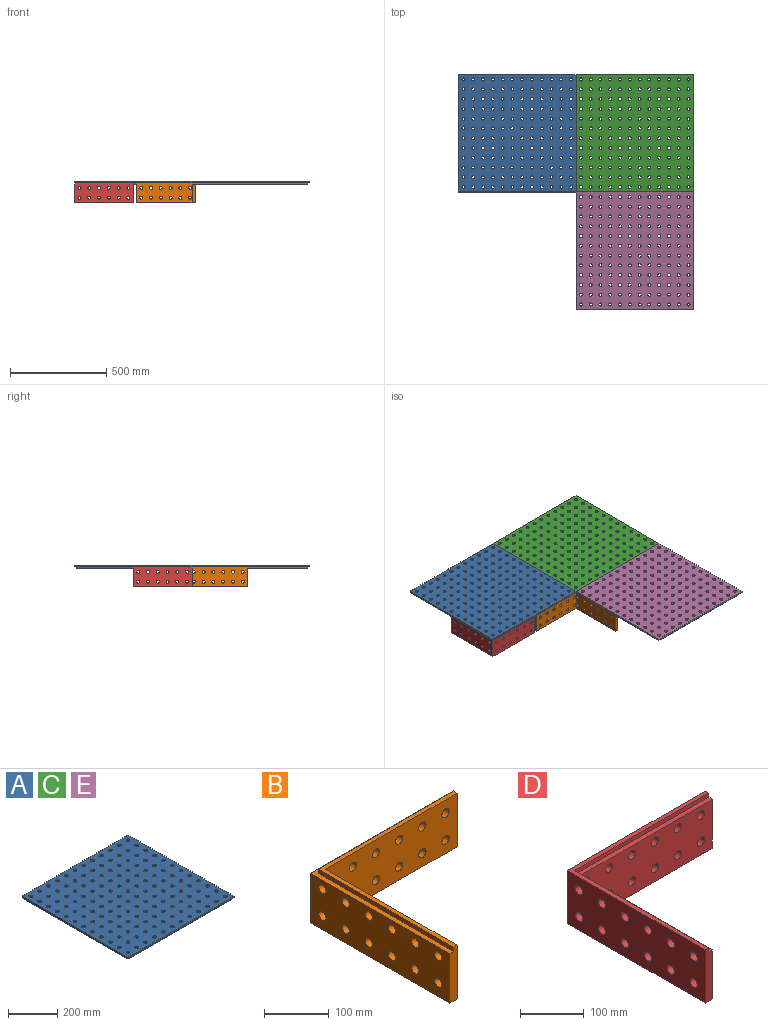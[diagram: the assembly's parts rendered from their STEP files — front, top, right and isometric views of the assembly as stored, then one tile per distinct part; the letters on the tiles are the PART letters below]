
ASSEMBLY  parts=5 mates=4
PART A: 155 faces, bbox 609.6x609.6x15.9 mm
  f0: plane 593.73x593.73mm, normal (0,0,-1), area 324007.1mm2, adj f6,f7,f8,f9,f10,f11,f12,f13
  f1: plane 609.6x7.94mm, normal (1,0,0), area 4838.7mm2, adj f2,f4,f5,f154
  f2: plane 609.6x7.94mm, normal (0,1,0), area 4838.7mm2, adj f1,f3,f5,f154
  f3: plane 609.6x7.94mm, normal (-1,0,0), area 4838.7mm2, adj f2,f4,f5,f154
  f4: plane 609.6x7.94mm, normal (0,-1,0), area 4838.7mm2, adj f1,f3,f5,f154
  f5: plane 609.6x609.6mm, normal (0,0,1), area 343109.9mm2, adj f1,f2,f3,f4,f6,f7,f8,f9
  f6: cylinder r=7.94mm len=15.88mm, axis (0,0,1), area 791.7mm2, adj f0,f5
  f7: cylinder r=7.94mm len=15.88mm, axis (0,0,1), area 791.7mm2, adj f0,f5
  f8: cylinder r=7.94mm len=15.88mm, axis (0,0,1), area 791.7mm2, adj f0,f5
  f9: cylinder r=7.94mm len=15.88mm, axis (0,0,1), area 791.7mm2, adj f0,f5
  f10: cylinder r=7.94mm len=15.88mm, axis (0,0,1), area 791.7mm2, adj f0,f5
  f11: cylinder r=7.94mm len=15.88mm, axis (0,0,1), area 791.7mm2, adj f0,f5
  f12: cylinder r=7.94mm len=15.88mm, axis (0,0,1), area 791.7mm2, adj f0,f5
  f13: cylinder r=7.94mm len=15.88mm, axis (0,0,1), area 791.7mm2, adj f0,f5
  f14: cylinder r=7.94mm len=15.88mm, axis (0,0,1), area 791.7mm2, adj f0,f5
  f15: cylinder r=7.94mm len=15.88mm, axis (0,0,1), area 791.7mm2, adj f0,f5
  f16: cylinder r=7.94mm len=15.88mm, axis (0,0,1), area 791.7mm2, adj f0,f5
  f17: cylinder r=7.94mm len=15.88mm, axis (0,0,1), area 791.7mm2, adj f0,f5
  f18: cylinder r=7.94mm len=15.88mm, axis (0,0,1), area 791.7mm2, adj f0,f5
  f19: cylinder r=7.94mm len=15.88mm, axis (0,0,1), area 791.7mm2, adj f0,f5
  f20: cylinder r=7.94mm len=15.88mm, axis (0,0,1), area 791.7mm2, adj f0,f5
  f21: cylinder r=7.94mm len=15.88mm, axis (0,0,1), area 791.7mm2, adj f0,f5
  f22: cylinder r=7.94mm len=15.88mm, axis (0,0,1), area 791.7mm2, adj f0,f5
  f23: cylinder r=7.94mm len=15.88mm, axis (0,0,1), area 791.7mm2, adj f0,f5
  f24: cylinder r=7.94mm len=15.88mm, axis (0,0,1), area 791.7mm2, adj f0,f5
  f25: cylinder r=7.94mm len=15.88mm, axis (0,0,1), area 791.7mm2, adj f0,f5
  f26: cylinder r=7.94mm len=15.88mm, axis (0,0,1), area 791.7mm2, adj f0,f5
  f27: cylinder r=7.94mm len=15.88mm, axis (0,0,1), area 791.7mm2, adj f0,f5
  f28: cylinder r=7.94mm len=15.88mm, axis (0,0,1), area 791.7mm2, adj f0,f5
  f29: cylinder r=7.94mm len=15.88mm, axis (0,0,1), area 791.7mm2, adj f0,f5
  f30: cylinder r=7.94mm len=15.88mm, axis (0,0,1), area 791.7mm2, adj f0,f5
  f31: cylinder r=7.94mm len=15.88mm, axis (0,0,1), area 791.7mm2, adj f0,f5
  f32: cylinder r=7.94mm len=15.88mm, axis (0,0,1), area 791.7mm2, adj f0,f5
  f33: cylinder r=7.94mm len=15.88mm, axis (0,0,1), area 791.7mm2, adj f0,f5
  f34: cylinder r=7.94mm len=15.88mm, axis (0,0,1), area 791.7mm2, adj f0,f5
  f35: cylinder r=7.94mm len=15.88mm, axis (0,0,1), area 791.7mm2, adj f0,f5
  f36: cylinder r=7.94mm len=15.88mm, axis (0,0,1), area 791.7mm2, adj f0,f5
  f37: cylinder r=7.94mm len=15.88mm, axis (0,0,1), area 791.7mm2, adj f0,f5
  f38: cylinder r=7.94mm len=15.88mm, axis (0,0,1), area 791.7mm2, adj f0,f5
  f39: cylinder r=7.94mm len=15.88mm, axis (0,0,1), area 791.7mm2, adj f0,f5
  f40: cylinder r=7.94mm len=15.88mm, axis (0,0,1), area 791.7mm2, adj f0,f5
  f41: cylinder r=7.94mm len=15.88mm, axis (0,0,1), area 791.7mm2, adj f0,f5
  f42: cylinder r=7.94mm len=15.88mm, axis (0,0,1), area 791.7mm2, adj f0,f5
  f43: cylinder r=7.94mm len=15.88mm, axis (0,0,1), area 791.7mm2, adj f0,f5
  f44: cylinder r=7.94mm len=15.88mm, axis (0,0,1), area 791.7mm2, adj f0,f5
  f45: cylinder r=7.94mm len=15.88mm, axis (0,0,1), area 791.7mm2, adj f0,f5
  f46: cylinder r=7.94mm len=15.88mm, axis (0,0,1), area 791.7mm2, adj f0,f5
  f47: cylinder r=7.94mm len=15.88mm, axis (0,0,1), area 791.7mm2, adj f0,f5
  f48: cylinder r=7.94mm len=15.88mm, axis (0,0,1), area 791.7mm2, adj f0,f5
  f49: cylinder r=7.94mm len=15.88mm, axis (0,0,1), area 791.7mm2, adj f0,f5
  f50: cylinder r=7.94mm len=15.88mm, axis (0,0,1), area 791.7mm2, adj f0,f5
  f51: cylinder r=7.94mm len=15.88mm, axis (0,0,1), area 791.7mm2, adj f0,f5
  f52: cylinder r=7.94mm len=15.88mm, axis (0,0,1), area 791.7mm2, adj f0,f5
  f53: cylinder r=7.94mm len=15.88mm, axis (0,0,1), area 791.7mm2, adj f0,f5
  f54: cylinder r=7.94mm len=15.88mm, axis (0,0,1), area 791.7mm2, adj f0,f5
  f55: cylinder r=7.94mm len=15.88mm, axis (0,0,1), area 791.7mm2, adj f0,f5
  f56: cylinder r=7.94mm len=15.88mm, axis (0,0,1), area 791.7mm2, adj f0,f5
  f57: cylinder r=7.94mm len=15.88mm, axis (0,0,1), area 791.7mm2, adj f0,f5
  f58: cylinder r=7.94mm len=15.88mm, axis (0,0,1), area 791.7mm2, adj f0,f5
  f59: cylinder r=7.94mm len=15.88mm, axis (0,0,1), area 791.7mm2, adj f0,f5
  f60: cylinder r=7.94mm len=15.88mm, axis (0,0,1), area 791.7mm2, adj f0,f5
  f61: cylinder r=7.94mm len=15.88mm, axis (0,0,1), area 791.7mm2, adj f0,f5
  f62: cylinder r=7.94mm len=15.88mm, axis (0,0,1), area 791.7mm2, adj f0,f5
  f63: cylinder r=7.94mm len=15.88mm, axis (0,0,1), area 791.7mm2, adj f0,f5
  f64: cylinder r=7.94mm len=15.88mm, axis (0,0,1), area 791.7mm2, adj f0,f5
  f65: cylinder r=7.94mm len=15.88mm, axis (0,0,1), area 791.7mm2, adj f0,f5
  f66: cylinder r=7.94mm len=15.88mm, axis (0,0,1), area 791.7mm2, adj f0,f5
  f67: cylinder r=7.94mm len=15.88mm, axis (0,0,1), area 791.7mm2, adj f0,f5
  f68: cylinder r=7.94mm len=15.88mm, axis (0,0,1), area 791.7mm2, adj f0,f5
  f69: cylinder r=7.94mm len=15.88mm, axis (0,0,1), area 791.7mm2, adj f0,f5
  f70: cylinder r=7.94mm len=15.88mm, axis (0,0,1), area 791.7mm2, adj f0,f5
  f71: cylinder r=7.94mm len=15.88mm, axis (0,0,1), area 791.7mm2, adj f0,f5
  f72: cylinder r=7.94mm len=15.88mm, axis (0,0,1), area 791.7mm2, adj f0,f5
  f73: cylinder r=7.94mm len=15.88mm, axis (0,0,1), area 791.7mm2, adj f0,f5
  f74: cylinder r=7.94mm len=15.88mm, axis (0,0,1), area 791.7mm2, adj f0,f5
  f75: cylinder r=7.94mm len=15.88mm, axis (0,0,1), area 791.7mm2, adj f0,f5
  f76: cylinder r=7.94mm len=15.88mm, axis (0,0,1), area 791.7mm2, adj f0,f5
  f77: cylinder r=7.94mm len=15.88mm, axis (0,0,1), area 791.7mm2, adj f0,f5
  f78: cylinder r=7.94mm len=15.88mm, axis (0,0,1), area 791.7mm2, adj f0,f5
  f79: cylinder r=7.94mm len=15.88mm, axis (0,0,1), area 791.7mm2, adj f0,f5
  f80: cylinder r=7.94mm len=15.88mm, axis (0,0,1), area 791.7mm2, adj f0,f5
  f81: cylinder r=7.94mm len=15.88mm, axis (0,0,1), area 791.7mm2, adj f0,f5
  f82: cylinder r=7.94mm len=15.88mm, axis (0,0,1), area 791.7mm2, adj f0,f5
  f83: cylinder r=7.94mm len=15.88mm, axis (0,0,1), area 791.7mm2, adj f0,f5
  f84: cylinder r=7.94mm len=15.88mm, axis (0,0,1), area 791.7mm2, adj f0,f5
  f85: cylinder r=7.94mm len=15.88mm, axis (0,0,1), area 791.7mm2, adj f0,f5
  f86: cylinder r=7.94mm len=15.88mm, axis (0,0,1), area 791.7mm2, adj f0,f5
  f87: cylinder r=7.94mm len=15.88mm, axis (0,0,1), area 791.7mm2, adj f0,f5
  f88: cylinder r=7.94mm len=15.88mm, axis (0,0,1), area 791.7mm2, adj f0,f5
  f89: cylinder r=7.94mm len=15.88mm, axis (0,0,1), area 791.7mm2, adj f0,f5
  f90: cylinder r=7.94mm len=15.88mm, axis (0,0,1), area 791.7mm2, adj f0,f5
  f91: cylinder r=7.94mm len=15.88mm, axis (0,0,1), area 791.7mm2, adj f0,f5
  f92: cylinder r=7.94mm len=15.88mm, axis (0,0,1), area 791.7mm2, adj f0,f5
  f93: cylinder r=7.94mm len=15.88mm, axis (0,0,1), area 791.7mm2, adj f0,f5
  f94: cylinder r=7.94mm len=15.88mm, axis (0,0,1), area 791.7mm2, adj f0,f5
  f95: cylinder r=7.94mm len=15.88mm, axis (0,0,1), area 791.7mm2, adj f0,f5
  f96: cylinder r=7.94mm len=15.88mm, axis (0,0,1), area 791.7mm2, adj f0,f5
  f97: cylinder r=7.94mm len=15.88mm, axis (0,0,1), area 791.7mm2, adj f0,f5
  f98: cylinder r=7.94mm len=15.88mm, axis (0,0,1), area 791.7mm2, adj f0,f5
  f99: cylinder r=7.94mm len=15.88mm, axis (0,0,1), area 791.7mm2, adj f0,f5
  f100: cylinder r=7.94mm len=15.88mm, axis (0,0,1), area 791.7mm2, adj f0,f5
  f101: cylinder r=7.94mm len=15.88mm, axis (0,0,1), area 791.7mm2, adj f0,f5
  f102: cylinder r=7.94mm len=15.88mm, axis (0,0,1), area 791.7mm2, adj f0,f5
  f103: cylinder r=7.94mm len=15.88mm, axis (0,0,1), area 791.7mm2, adj f0,f5
  f104: cylinder r=7.94mm len=15.88mm, axis (0,0,1), area 791.7mm2, adj f0,f5
  f105: cylinder r=7.94mm len=15.88mm, axis (0,0,1), area 791.7mm2, adj f0,f5
  f106: cylinder r=7.94mm len=15.88mm, axis (0,0,1), area 791.7mm2, adj f0,f5
  f107: cylinder r=7.94mm len=15.88mm, axis (0,0,1), area 791.7mm2, adj f0,f5
  f108: cylinder r=7.94mm len=15.88mm, axis (0,0,1), area 791.7mm2, adj f0,f5
  f109: cylinder r=7.94mm len=15.88mm, axis (0,0,1), area 791.7mm2, adj f0,f5
  f110: cylinder r=7.94mm len=15.88mm, axis (0,0,1), area 791.7mm2, adj f0,f5
  f111: cylinder r=7.94mm len=15.88mm, axis (0,0,1), area 791.7mm2, adj f0,f5
  f112: cylinder r=7.94mm len=15.88mm, axis (0,0,1), area 791.7mm2, adj f0,f5
  f113: cylinder r=7.94mm len=15.88mm, axis (0,0,1), area 791.7mm2, adj f0,f5
  f114: cylinder r=7.94mm len=15.88mm, axis (0,0,1), area 791.7mm2, adj f0,f5
  f115: cylinder r=7.94mm len=15.88mm, axis (0,0,1), area 791.7mm2, adj f0,f5
  f116: cylinder r=7.94mm len=15.88mm, axis (0,0,1), area 791.7mm2, adj f0,f5
  f117: cylinder r=7.94mm len=15.88mm, axis (0,0,1), area 791.7mm2, adj f0,f5
  f118: cylinder r=7.94mm len=15.88mm, axis (0,0,1), area 791.7mm2, adj f0,f5
  f119: cylinder r=7.94mm len=15.88mm, axis (0,0,1), area 791.7mm2, adj f0,f5
  f120: cylinder r=7.94mm len=15.88mm, axis (0,0,1), area 791.7mm2, adj f0,f5
  f121: cylinder r=7.94mm len=15.88mm, axis (0,0,1), area 791.7mm2, adj f0,f5
  f122: cylinder r=7.94mm len=15.88mm, axis (0,0,1), area 791.7mm2, adj f0,f5
  f123: cylinder r=7.94mm len=15.88mm, axis (0,0,1), area 791.7mm2, adj f0,f5
  f124: cylinder r=7.94mm len=15.88mm, axis (0,0,1), area 791.7mm2, adj f0,f5
  f125: cylinder r=7.94mm len=15.88mm, axis (0,0,1), area 791.7mm2, adj f0,f5
  f126: cylinder r=7.94mm len=15.88mm, axis (0,0,1), area 791.7mm2, adj f0,f5
  f127: cylinder r=7.94mm len=15.88mm, axis (0,0,1), area 791.7mm2, adj f0,f5
  f128: cylinder r=7.94mm len=15.88mm, axis (0,0,1), area 791.7mm2, adj f0,f5
  f129: cylinder r=7.94mm len=15.88mm, axis (0,0,1), area 791.7mm2, adj f0,f5
  f130: cylinder r=7.94mm len=15.88mm, axis (0,0,1), area 791.7mm2, adj f0,f5
  f131: cylinder r=7.94mm len=15.88mm, axis (0,0,1), area 791.7mm2, adj f0,f5
  f132: cylinder r=7.94mm len=15.88mm, axis (0,0,1), area 791.7mm2, adj f0,f5
  f133: cylinder r=7.94mm len=15.88mm, axis (0,0,1), area 791.7mm2, adj f0,f5
  f134: cylinder r=7.94mm len=15.88mm, axis (0,0,1), area 791.7mm2, adj f0,f5
  f135: cylinder r=7.94mm len=15.88mm, axis (0,0,1), area 791.7mm2, adj f0,f5
  f136: cylinder r=7.94mm len=15.88mm, axis (0,0,1), area 791.7mm2, adj f0,f5
  f137: cylinder r=7.94mm len=15.88mm, axis (0,0,1), area 791.7mm2, adj f0,f5
  f138: cylinder r=7.94mm len=15.88mm, axis (0,0,1), area 791.7mm2, adj f0,f5
  f139: cylinder r=7.94mm len=15.88mm, axis (0,0,1), area 791.7mm2, adj f0,f5
  f140: cylinder r=7.94mm len=15.88mm, axis (0,0,1), area 791.7mm2, adj f0,f5
  f141: cylinder r=7.94mm len=15.88mm, axis (0,0,1), area 791.7mm2, adj f0,f5
  f142: cylinder r=7.94mm len=15.88mm, axis (0,0,1), area 791.7mm2, adj f0,f5
  f143: cylinder r=7.94mm len=15.88mm, axis (0,0,1), area 791.7mm2, adj f0,f5
  f144: cylinder r=7.94mm len=15.88mm, axis (0,0,1), area 791.7mm2, adj f0,f5
  f145: cylinder r=7.94mm len=15.88mm, axis (0,0,1), area 791.7mm2, adj f0,f5
  f146: cylinder r=7.94mm len=15.88mm, axis (0,0,1), area 791.7mm2, adj f0,f5
  f147: cylinder r=7.94mm len=15.88mm, axis (0,0,1), area 791.7mm2, adj f0,f5
  f148: cylinder r=7.94mm len=15.88mm, axis (0,0,1), area 791.7mm2, adj f0,f5
  f149: cylinder r=7.94mm len=15.88mm, axis (0,0,1), area 791.7mm2, adj f0,f5
  f150: plane 593.73x7.94mm, normal (0,-1,0), area 4712.7mm2, adj f0,f151,f153,f154
  f151: plane 593.73x7.94mm, normal (1,0,0), area 4712.7mm2, adj f0,f150,f152,f154
  f152: plane 593.73x7.94mm, normal (0,1,0), area 4712.7mm2, adj f0,f151,f153,f154
  f153: plane 593.73x7.94mm, normal (-1,0,0), area 4712.7mm2, adj f0,f150,f152,f154
  f154: plane 609.6x609.6mm, normal (0,0,-1), area 19102.8mm2, adj f1,f2,f3,f4,f150,f151,f152,f153
PART B: 35 faces, bbox 304.8x304.8x101.6 mm
  f0: plane 304.8x93.66mm, normal (0,1,0), area 26173.1mm2, adj f1,f3,f7,f20,f21,f22,f23,f24
  f1: plane 304.8x93.66mm, normal (-1,0,0), area 26173.1mm2, adj f0,f4,f7,f8,f9,f10,f11,f12
  f2: plane 296.86x296.86mm, normal (0,0,1), area 4649.7mm2, adj f3,f4,f5,f6,f32,f33
  f3: plane 101.6x15.88mm, normal (1,0,0), area 1549.9mm2, adj f0,f2,f6,f7,f33,f34
  f4: plane 101.6x15.88mm, normal (0,-1,0), area 1549.9mm2, adj f1,f2,f5,f7,f32,f34
  f5: plane 288.93x101.6mm, normal (1,0,0), area 26979.6mm2, adj f2,f4,f6,f7,f8,f9,f10,f11
  f6: plane 288.93x101.6mm, normal (0,-1,0), area 26979.6mm2, adj f2,f3,f5,f7,f20,f21,f22,f23
  f7: plane 304.8x304.8mm, normal (0,0,-1), area 9425.4mm2, adj f0,f1,f3,f4,f5,f6
  f8: cylinder r=7.94mm len=15.88mm, axis (-1,0,0), area 791.7mm2, adj f1,f5
  f9: cylinder r=7.94mm len=15.88mm, axis (-1,0,0), area 791.7mm2, adj f1,f5
  f10: cylinder r=7.94mm len=15.88mm, axis (-1,0,0), area 791.7mm2, adj f1,f5
  f11: cylinder r=7.94mm len=15.88mm, axis (-1,0,0), area 791.7mm2, adj f1,f5
  f12: cylinder r=7.94mm len=15.88mm, axis (-1,0,0), area 791.7mm2, adj f1,f5
  f13: cylinder r=7.94mm len=15.88mm, axis (-1,0,0), area 791.7mm2, adj f1,f5
  f14: cylinder r=7.94mm len=15.88mm, axis (-1,0,0), area 791.7mm2, adj f1,f5
  f15: cylinder r=7.94mm len=15.88mm, axis (-1,0,0), area 791.7mm2, adj f1,f5
  f16: cylinder r=7.94mm len=15.88mm, axis (-1,0,0), area 791.7mm2, adj f1,f5
  f17: cylinder r=7.94mm len=15.88mm, axis (-1,0,0), area 791.7mm2, adj f1,f5
  f18: cylinder r=7.94mm len=15.88mm, axis (-1,0,0), area 791.7mm2, adj f1,f5
  f19: cylinder r=7.94mm len=15.88mm, axis (-1,0,0), area 791.7mm2, adj f1,f5
  f20: cylinder r=7.94mm len=15.88mm, axis (0,1,0), area 791.7mm2, adj f0,f6
  f21: cylinder r=7.94mm len=15.88mm, axis (0,1,0), area 791.7mm2, adj f0,f6
  f22: cylinder r=7.94mm len=15.88mm, axis (0,1,0), area 791.7mm2, adj f0,f6
  f23: cylinder r=7.94mm len=15.88mm, axis (0,1,0), area 791.7mm2, adj f0,f6
  f24: cylinder r=7.94mm len=15.88mm, axis (0,1,0), area 791.7mm2, adj f0,f6
  f25: cylinder r=7.94mm len=15.88mm, axis (0,1,0), area 791.7mm2, adj f0,f6
  f26: cylinder r=7.94mm len=15.88mm, axis (0,1,0), area 791.7mm2, adj f0,f6
  f27: cylinder r=7.94mm len=15.88mm, axis (0,1,0), area 791.7mm2, adj f0,f6
  f28: cylinder r=7.94mm len=15.88mm, axis (0,1,0), area 791.7mm2, adj f0,f6
  f29: cylinder r=7.94mm len=15.88mm, axis (0,1,0), area 791.7mm2, adj f0,f6
  f30: cylinder r=7.94mm len=15.88mm, axis (0,1,0), area 791.7mm2, adj f0,f6
  f31: cylinder r=7.94mm len=15.88mm, axis (0,1,0), area 791.7mm2, adj f0,f6
  f32: plane 296.86x7.94mm, normal (-1,0,0), area 2356.3mm2, adj f2,f4,f33,f34
  f33: plane 296.86x7.94mm, normal (0,1,0), area 2356.3mm2, adj f2,f3,f32,f34
  f34: plane 304.8x304.8mm, normal (0,0,1), area 4775.7mm2, adj f0,f1,f3,f4,f32,f33
PART C: same geometry as A
PART D: 35 faces, bbox 304.8x304.8x101.6 mm
  f0: plane 101.6x15.88mm, normal (1,0,0), area 1549.9mm2, adj f2,f3,f6,f7,f32,f34
  f1: plane 288.93x93.66mm, normal (1,0,0), area 24686.2mm2, adj f2,f5,f7,f8,f9,f10,f11,f12
  f2: plane 288.93x93.66mm, normal (0,-1,0), area 24686.2mm2, adj f0,f1,f7,f20,f21,f22,f23,f24
  f3: plane 304.8x101.6mm, normal (0,1,0), area 28592.5mm2, adj f0,f4,f6,f7,f20,f21,f22,f23
  f4: plane 304.8x101.6mm, normal (-1,0,0), area 28592.5mm2, adj f3,f5,f6,f7,f8,f9,f10,f11
  f5: plane 101.6x15.88mm, normal (0,-1,0), area 1549.9mm2, adj f1,f4,f6,f7,f33,f34
  f6: plane 304.8x304.8mm, normal (0,0,1), area 4775.7mm2, adj f0,f3,f4,f5,f32,f33
  f7: plane 304.8x304.8mm, normal (0,0,-1), area 9425.4mm2, adj f0,f1,f2,f3,f4,f5
  f8: cylinder r=7.94mm len=15.88mm, axis (-1,0,0), area 791.7mm2, adj f1,f4
  f9: cylinder r=7.94mm len=15.88mm, axis (-1,0,0), area 791.7mm2, adj f1,f4
  f10: cylinder r=7.94mm len=15.88mm, axis (-1,0,0), area 791.7mm2, adj f1,f4
  f11: cylinder r=7.94mm len=15.88mm, axis (-1,0,0), area 791.7mm2, adj f1,f4
  f12: cylinder r=7.94mm len=15.88mm, axis (-1,0,0), area 791.7mm2, adj f1,f4
  f13: cylinder r=7.94mm len=15.88mm, axis (-1,0,0), area 791.7mm2, adj f1,f4
  f14: cylinder r=7.94mm len=15.88mm, axis (-1,0,0), area 791.7mm2, adj f1,f4
  f15: cylinder r=7.94mm len=15.88mm, axis (-1,0,0), area 791.7mm2, adj f1,f4
  f16: cylinder r=7.94mm len=15.88mm, axis (-1,0,0), area 791.7mm2, adj f1,f4
  f17: cylinder r=7.94mm len=15.88mm, axis (-1,0,0), area 791.7mm2, adj f1,f4
  f18: cylinder r=7.94mm len=15.88mm, axis (-1,0,0), area 791.7mm2, adj f1,f4
  f19: cylinder r=7.94mm len=15.88mm, axis (-1,0,0), area 791.7mm2, adj f1,f4
  f20: cylinder r=7.94mm len=15.88mm, axis (0,1,0), area 791.7mm2, adj f2,f3
  f21: cylinder r=7.94mm len=15.88mm, axis (0,1,0), area 791.7mm2, adj f2,f3
  f22: cylinder r=7.94mm len=15.88mm, axis (0,1,0), area 791.7mm2, adj f2,f3
  f23: cylinder r=7.94mm len=15.88mm, axis (0,1,0), area 791.7mm2, adj f2,f3
  f24: cylinder r=7.94mm len=15.88mm, axis (0,1,0), area 791.7mm2, adj f2,f3
  f25: cylinder r=7.94mm len=15.88mm, axis (0,1,0), area 791.7mm2, adj f2,f3
  f26: cylinder r=7.94mm len=15.88mm, axis (0,1,0), area 791.7mm2, adj f2,f3
  f27: cylinder r=7.94mm len=15.88mm, axis (0,1,0), area 791.7mm2, adj f2,f3
  f28: cylinder r=7.94mm len=15.88mm, axis (0,1,0), area 791.7mm2, adj f2,f3
  f29: cylinder r=7.94mm len=15.88mm, axis (0,1,0), area 791.7mm2, adj f2,f3
  f30: cylinder r=7.94mm len=15.88mm, axis (0,1,0), area 791.7mm2, adj f2,f3
  f31: cylinder r=7.94mm len=15.88mm, axis (0,1,0), area 791.7mm2, adj f2,f3
  f32: plane 296.86x7.94mm, normal (0,-1,0), area 2356.3mm2, adj f0,f6,f33,f34
  f33: plane 296.86x7.94mm, normal (1,0,0), area 2356.3mm2, adj f5,f6,f32,f34
  f34: plane 296.86x296.86mm, normal (0,0,1), area 4649.7mm2, adj f0,f1,f2,f5,f32,f33
PART E: same geometry as A
PLACE A t=(-653.14,119.29,566.75)mm
PLACE B rot(axis=(0,0,-1),90deg) t=(-332.46,-169.63,473.09)mm
PLACE C t=(-43.54,119.29,566.75)mm
PLACE D rot(axis=(0,0,1),90deg) t=(-957.94,-185.51,473.09)mm
PLACE E t=(-43.54,-490.31,566.75)mm
MATE fastened E.f154 <-> B.f2  axis (0,0,-1) through (-348.34,-185.51,574.69)mm
MATE fastened E.f5 <-> C.f5  axis (0,0,1) through (-348.34,-185.51,582.63)mm
MATE fastened A.f5 <-> C.f5  axis (0,0,1) through (-348.34,-185.51,582.63)mm
MATE fastened D.f6 <-> A.f154  axis (0,0,1) through (-957.94,-185.51,574.69)mm
